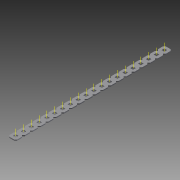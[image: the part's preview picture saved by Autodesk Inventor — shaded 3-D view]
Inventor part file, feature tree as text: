
AUTODESK INVENTOR PART (.ipt)
format: ipt  version: 2015 SP1 (Build 190203100, 203)  size: 1,119,744 bytes
history: native  units: in
note: dims shown in document units (in); Inventor stores cm internally (conversion verified against a paired STEP export)
features: other x29, extrude x2, pattern_linear x1, imported_body x1
ambient origin geometry x8: Origin, YZ Plane, XZ Plane, XY Plane, X Axis, Y Axis, Z Axis, Center Point
bodies: Body1 (feature_tree)
feature tree (33):
  other  "Diamond-Pattern"
  other  "Plate"
  extrude  "length cut"  TaperAngle=0.0deg  [1 undecoded]
  extrude  "width cut"  TaperAngle=0.0deg  [1 undecoded]
  other  "constraint axis"
  pattern_linear  "constraint axes"  Spacing1=0.5in  [1 undecoded]
  other  "front plane"
  other  "right plane"
  imported_body  "Base1"
  other  "length profile"
  other  "width profile"
  other  "Work Point1"
  other  "back plane"
  other  "left plane"
  other  "Work Axis170"
  other  "Work Axis171"
  other  "Work Axis172"
  other  "Work Axis173"
  other  "Work Axis174"
  other  "Work Axis175"
  other  "Work Axis176"
  other  "Work Axis177"
  other  "Work Axis178"
  other  "Work Axis229"
  other  "Work Axis230"
  other  "Work Axis231"
  other  "Work Axis232"
  other  "Work Axis233"
  other  "Work Axis234"
  other  "Work Axis235"
  other  "Work Axis236"
  other  "Work Axis237"
  other  "Work Axis238"
note: 3 required parameter values undecoded (feature->parameter linkage not recoverable at this tier; creation-order binding heuristic only, values carry confidence <= 0.55)
